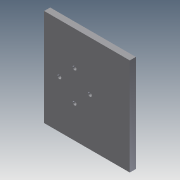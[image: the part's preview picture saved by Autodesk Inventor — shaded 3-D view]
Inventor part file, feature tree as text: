
AUTODESK INVENTOR PART (.ipt)
format: ipt  version: 2011 (Build 150239000, 239)  size: 90,624 bytes
history: native  units: in
note: dims shown in document units (in); Inventor stores cm internally (conversion verified against a paired STEP export)
features: extrude x3, sketch x3
ambient origin geometry x8: Origin, YZ Plane, XZ Plane, XY Plane, X Axis, Y Axis, Z Axis, Center Point
bodies: Solid1 (feature_tree)
feature tree (6):
  extrude  "Extrusion1"  Depth=2.0079in
  extrude  "Extrusion2"  Depth=0.9843in
  extrude  "Extrusion3"  Depth=0.0787in
  sketch  "Sketch1"  dims[d0=1.7717in d1=2.0079in]
  sketch  "Sketch2"  dims[d2=0.125in d3=0.0in d4=0.9843in]
  sketch  "Sketch3"  dims[d6=0.6299in d7=0.0787in d8=0.0787in d9=0.0787in d10=0.0787in d11=0.6299in d12=1.0in d13=0.0in d14=0.156in d15=1.0in d16=0.0in]
